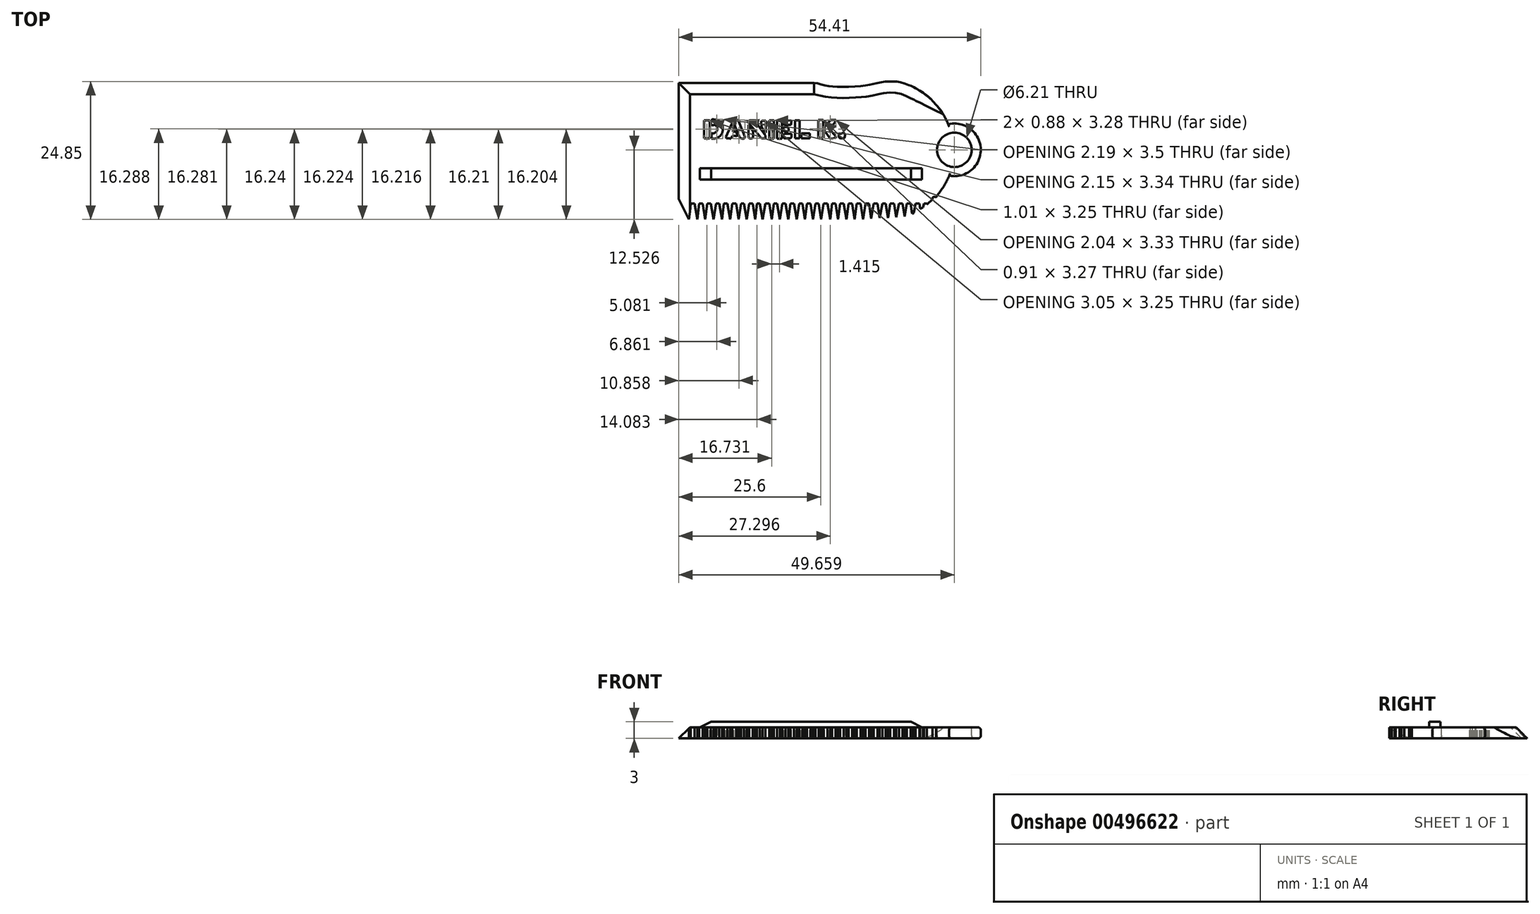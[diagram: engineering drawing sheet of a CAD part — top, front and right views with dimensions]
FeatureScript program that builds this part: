
annotation { "Feature Type Name" : "Feature", "Feature Type Description" : "" }
export const myFeature = defineFeature(function(context is Context, id is Id, definition is map)
    precondition{}
    {
        {
            var Q0;
            Q0=qCreatedBy(makeId("Top.planeOp"),FACE);
            var sketch = newSketch(context, id + "F0", { "sketchPlane" : qUnion([Q0])});
            skLineSegment(sketch, "E0", {"start": v(1.4, 38.48) * mm, "end": v(1.4, 17.59) * mm});
            skLineSegment(sketch, "E1", {"start": v(1.4, 17.59) * mm, "end": v(3.24, 13.91) * mm});
            skLineSegment(sketch, "E2", {"start": v(3.24, 13.91) * mm, "end": v(3.59, 16.75) * mm});
            skLineSegment(sketch, "E3", {"start": v(3.59, 16.75) * mm, "end": v(4.26, 16.75) * mm});
            skLineSegment(sketch, "E4", {"start": v(4.26, 16.75) * mm, "end": v(4.74, 13.91) * mm});
            skLineSegment(sketch, "E5", {"start": v(4.74, 13.91) * mm, "end": v(5.11, 16.75) * mm});
            skLineSegment(sketch, "E6", {"start": v(5.11, 16.75) * mm, "end": v(5.73, 16.75) * mm});
            skLineSegment(sketch, "E7", {"start": v(5.73, 16.75) * mm, "end": v(6.2, 13.91) * mm});
            skLineSegment(sketch, "E8", {"start": v(6.2, 13.91) * mm, "end": v(6.56, 16.75) * mm});
            skLineSegment(sketch, "E9", {"start": v(6.56, 16.75) * mm, "end": v(7.2, 16.75) * mm});
            skLineSegment(sketch, "E10", {"start": v(7.2, 16.75) * mm, "end": v(7.71, 13.91) * mm});
            skLineSegment(sketch, "E11", {"start": v(7.71, 13.91) * mm, "end": v(8.14, 16.75) * mm});
            skLineSegment(sketch, "E12", {"start": v(8.14, 16.75) * mm, "end": v(8.7, 16.75) * mm});
            skLineSegment(sketch, "E13", {"start": v(8.7, 16.75) * mm, "end": v(9.2, 13.91) * mm});
            skLineSegment(sketch, "E14", {"start": v(9.2, 13.91) * mm, "end": v(9.56, 16.75) * mm});
            skLineSegment(sketch, "E15", {"start": v(9.56, 16.75) * mm, "end": v(10.18, 16.75) * mm});
            skLineSegment(sketch, "E16", {"start": v(10.18, 16.75) * mm, "end": v(10.7, 13.91) * mm});
            skLineSegment(sketch, "E17", {"start": v(10.7, 13.91) * mm, "end": v(11.07, 16.75) * mm});
            skLineSegment(sketch, "E18", {"start": v(11.07, 16.75) * mm, "end": v(11.75, 16.75) * mm});
            skLineSegment(sketch, "E19", {"start": v(11.75, 16.75) * mm, "end": v(12.19, 13.91) * mm});
            skLineSegment(sketch, "E20", {"start": v(12.19, 13.91) * mm, "end": v(12.62, 16.75) * mm});
            skLineSegment(sketch, "E21", {"start": v(12.62, 16.75) * mm, "end": v(13.15, 16.75) * mm});
            skLineSegment(sketch, "E22", {"start": v(13.15, 16.75) * mm, "end": v(13.65, 13.91) * mm});
            skLineSegment(sketch, "E23", {"start": v(13.65, 13.91) * mm, "end": v(14.08, 16.75) * mm});
            skLineSegment(sketch, "E24", {"start": v(14.08, 16.75) * mm, "end": v(14.73, 16.75) * mm});
            skLineSegment(sketch, "E25", {"start": v(14.73, 16.75) * mm, "end": v(15.17, 13.91) * mm});
            skLineSegment(sketch, "E26", {"start": v(15.17, 13.91) * mm, "end": v(15.5, 16.75) * mm});
            skLineSegment(sketch, "E27", {"start": v(15.5, 16.75) * mm, "end": v(16.04, 16.75) * mm});
            skLineSegment(sketch, "E28", {"start": v(16.04, 16.75) * mm, "end": v(16.54, 13.91) * mm});
            skLineSegment(sketch, "E29", {"start": v(16.54, 13.91) * mm, "end": v(17.03, 16.75) * mm});
            skLineSegment(sketch, "E30", {"start": v(17.03, 16.75) * mm, "end": v(17.72, 16.75) * mm});
            skLineSegment(sketch, "E31", {"start": v(17.72, 16.75) * mm, "end": v(18.19, 13.91) * mm});
            skLineSegment(sketch, "E32", {"start": v(18.19, 13.91) * mm, "end": v(18.52, 16.75) * mm});
            skLineSegment(sketch, "E33", {"start": v(18.52, 16.75) * mm, "end": v(19.15, 16.75) * mm});
            skLineSegment(sketch, "E34", {"start": v(19.15, 16.75) * mm, "end": v(19.66, 13.91) * mm});
            skLineSegment(sketch, "E35", {"start": v(19.66, 13.91) * mm, "end": v(20.08, 16.75) * mm});
            skLineSegment(sketch, "E36", {"start": v(20.08, 16.75) * mm, "end": v(20.65, 16.75) * mm});
            skLineSegment(sketch, "E37", {"start": v(20.65, 16.75) * mm, "end": v(21.13, 13.91) * mm});
            skLineSegment(sketch, "E38", {"start": v(21.13, 13.91) * mm, "end": v(21.56, 16.75) * mm});
            skLineSegment(sketch, "E39", {"start": v(21.56, 16.75) * mm, "end": v(22.17, 16.75) * mm});
            skLineSegment(sketch, "E40", {"start": v(22.17, 16.75) * mm, "end": v(22.67, 13.91) * mm});
            skLineSegment(sketch, "E41", {"start": v(22.67, 13.91) * mm, "end": v(23.1, 16.75) * mm});
            skLineSegment(sketch, "E42", {"start": v(23.1, 16.75) * mm, "end": v(23.68, 16.75) * mm});
            skLineSegment(sketch, "E43", {"start": v(23.68, 16.75) * mm, "end": v(24.12, 13.91) * mm});
            skLineSegment(sketch, "E44", {"start": v(24.12, 13.91) * mm, "end": v(24.54, 16.75) * mm});
            skLineSegment(sketch, "E45", {"start": v(24.54, 16.75) * mm, "end": v(25.15, 16.75) * mm});
            skLineSegment(sketch, "E46", {"start": v(25.15, 16.75) * mm, "end": v(25.59, 13.91) * mm});
            skLineSegment(sketch, "E47", {"start": v(25.59, 13.91) * mm, "end": v(26.01, 16.75) * mm});
            skLineSegment(sketch, "E48", {"start": v(26.01, 16.75) * mm, "end": v(26.63, 16.75) * mm});
            skLineSegment(sketch, "E49", {"start": v(26.63, 16.75) * mm, "end": v(27.06, 13.91) * mm});
            skLineSegment(sketch, "E50", {"start": v(27.06, 13.91) * mm, "end": v(27.49, 16.75) * mm});
            skLineSegment(sketch, "E51", {"start": v(27.49, 16.75) * mm, "end": v(28.19, 16.75) * mm});
            skLineSegment(sketch, "E52", {"start": v(28.19, 16.75) * mm, "end": v(28.7, 13.91) * mm});
            skLineSegment(sketch, "E53", {"start": v(28.7, 13.91) * mm, "end": v(29.03, 16.75) * mm});
            skLineSegment(sketch, "E54", {"start": v(29.03, 16.75) * mm, "end": v(29.65, 16.75) * mm});
            skLineSegment(sketch, "E55", {"start": v(29.65, 16.75) * mm, "end": v(30.09, 13.91) * mm});
            skLineSegment(sketch, "E56", {"start": v(30.09, 13.91) * mm, "end": v(30.51, 16.75) * mm});
            skLineSegment(sketch, "E57", {"start": v(30.51, 16.75) * mm, "end": v(31.1, 16.75) * mm});
            skLineSegment(sketch, "E58", {"start": v(31.1, 16.75) * mm, "end": v(31.62, 13.91) * mm});
            skLineSegment(sketch, "E59", {"start": v(31.62, 13.91) * mm, "end": v(32.04, 16.75) * mm});
            skLineSegment(sketch, "E60", {"start": v(32.04, 16.75) * mm, "end": v(32.65, 16.75) * mm});
            skLineSegment(sketch, "E61", {"start": v(32.65, 16.75) * mm, "end": v(33.08, 13.91) * mm});
            skLineSegment(sketch, "E62", {"start": v(33.08, 13.91) * mm, "end": v(33.5, 16.75) * mm});
            skLineSegment(sketch, "E63", {"start": v(33.5, 16.75) * mm, "end": v(34.2, 16.75) * mm});
            skLineSegment(sketch, "E64", {"start": v(34.2, 16.75) * mm, "end": v(34.64, 13.91) * mm});
            skLineSegment(sketch, "E65", {"start": v(34.64, 13.91) * mm, "end": v(35.07, 16.75) * mm});
            skLineSegment(sketch, "E66", {"start": v(35.07, 16.75) * mm, "end": v(35.67, 16.75) * mm});
            skLineSegment(sketch, "E67", {"start": v(35.67, 16.75) * mm, "end": v(36.09, 14.06) * mm});
            skLineSegment(sketch, "E68", {"start": v(36.09, 14.06) * mm, "end": v(36.54, 16.75) * mm});
            skLineSegment(sketch, "E69", {"start": v(36.54, 16.75) * mm, "end": v(37.2, 16.75) * mm});
            skLineSegment(sketch, "E70", {"start": v(37.2, 16.75) * mm, "end": v(37.6, 14.13) * mm});
            skLineSegment(sketch, "E71", {"start": v(37.6, 14.13) * mm, "end": v(38.1, 16.75) * mm});
            skLineSegment(sketch, "E72", {"start": v(38.1, 16.75) * mm, "end": v(38.7, 16.75) * mm});
            skLineSegment(sketch, "E73", {"start": v(38.7, 16.75) * mm, "end": v(39.13, 14.13) * mm});
            skLineSegment(sketch, "E74", {"start": v(39.13, 14.13) * mm, "end": v(39.53, 16.75) * mm});
            skLineSegment(sketch, "E75", {"start": v(39.53, 16.75) * mm, "end": v(40.22, 16.75) * mm});
            skLineSegment(sketch, "E76", {"start": v(40.22, 16.75) * mm, "end": v(40.56, 14.29) * mm});
            skLineSegment(sketch, "E77", {"start": v(40.56, 14.29) * mm, "end": v(41.08, 16.75) * mm});
            skLineSegment(sketch, "E78", {"start": v(41.08, 16.75) * mm, "end": v(41.73, 16.75) * mm});
            skLineSegment(sketch, "E79", {"start": v(41.73, 16.75) * mm, "end": v(42.09, 14.41) * mm});
            skLineSegment(sketch, "E80", {"start": v(42.09, 14.41) * mm, "end": v(42.47, 16.75) * mm});
            skLineSegment(sketch, "E81", {"start": v(42.47, 16.75) * mm, "end": v(43.17, 16.75) * mm});
            skLineSegment(sketch, "E82", {"start": v(43.17, 16.75) * mm, "end": v(43.44, 14.9) * mm});
            skLineSegment(sketch, "E83", {"start": v(43.44, 14.9) * mm, "end": v(43.76, 15.1) * mm});
            skLineSegment(sketch, "E84", {"start": v(43.76, 15.1) * mm, "end": v(44.08, 16.75) * mm});
            skLineSegment(sketch, "E85", {"start": v(44.08, 16.75) * mm, "end": v(44.76, 16.75) * mm});
            skLineSegment(sketch, "E86", {"start": v(44.76, 16.75) * mm, "end": v(44.93, 15.78) * mm});
            skLineSegment(sketch, "E87", {"start": v(44.93, 15.78) * mm, "end": v(45.44, 16.08) * mm});
            skLineSegment(sketch, "E88", {"start": v(45.44, 16.08) * mm, "end": v(45.57, 16.75) * mm});
            skLineSegment(sketch, "E89", {"start": v(45.57, 16.75) * mm, "end": v(46.13, 16.75) * mm});
            skLineSegment(sketch, "E90", {"start": v(46.13, 16.75) * mm, "end": v(46.14, 16.6) * mm});
            skLineSegment(sketch, "E91", {"start": v(46.14, 16.6) * mm, "end": v(47.16, 17.52) * mm});
            skFitSpline(sketch, "E92", {"points": [v(1.4, 38.48) * mm, v(25.8, 38.48) * mm], "startDerivative": vector(24.39, 0) * mm, "endDerivative": vector(24.39, 0) * mm});
            skFitSpline(sketch, "E93", {"points": [v(25.8, 38.48) * mm, v(26.58, 38.37) * mm, v(27.86, 38) * mm, v(28.99, 37.85) * mm, v(30.77, 37.77) * mm, v(33.35, 37.86) * mm, v(35.53, 38.11) * mm, v(37.69, 38.6) * mm, v(39.09, 38.74) * mm, v(40.12, 38.76) * mm, v(41.15, 38.65) * mm, v(42.64, 38.2) * mm, v(43.17, 37.98) * mm, v(43.74, 37.71) * mm], "startDerivative": vector(12.37, -1.09) * mm, "endDerivative": vector(11.2, -5.59) * mm});
            skFitSpline(sketch, "E94", {"points": [v(43.74, 37.71) * mm, v(44.4, 37.35) * mm, v(45.39, 36.71) * mm, v(46.72, 35.7) * mm, v(47.62, 34.73) * mm, v(48.45, 33.74) * mm, v(49.36, 32.3) * mm, v(50.43, 29.83) * mm, v(51.02, 26.47) * mm, v(50.52, 22.9) * mm, v(49.43, 20.3) * mm, v(47.83, 18) * mm], "startDerivative": vector(11.48, -6.03) * mm, "endDerivative": vector(-15.82, -21.1) * mm});
            skFitSpline(sketch, "E95", {"points": [v(47.83, 18) * mm, v(47.76, 17.93) * mm], "startDerivative": vector(-0.07, -0.07) * mm, "endDerivative": vector(-0.07, -0.07) * mm});
            skFitSpline(sketch, "E96", {"points": [v(47.76, 17.93) * mm, v(47.6, 17.94) * mm, v(47.35, 17.95) * mm, v(47.23, 17.91) * mm, v(47.16, 17.82) * mm, v(47.15, 17.72) * mm, v(47.15, 17.6) * mm, v(47.16, 17.52) * mm], "startDerivative": vector(-0.96, 0.1) * mm, "endDerivative": vector(0.06, -0.72) * mm});
            skSolve(sketch);
        }
        {
            var Q0;
            Q0 = qSketchRegion(id + "F0", true);
            extrude(context, id + "F1", {"entities" : qUnion([Q0]), "depth" : 2 * mm, "offsetDistance" : 25 * mm});
        }
        {
            var Q0;
            Q0=makeQuery(id+"F1.opExtrude","CAP_EDGE",EDGE,{"disambiguationData":[OSD([sQuery(id+"F0.wireOp",EDGE,"E0")])],"isStart":false});
            var Q1;
            Q1=makeQuery(id+"F1.opExtrude","CAP_EDGE",EDGE,{"disambiguationData":[OSD([sQuery(id+"F0.wireOp",EDGE,"E92")])],"isStart":false});
            chamfer(context, id + "F2", {"entities" : qUnion([Q0, Q1]), "chamferType" : ChamferType.TWO_OFFSETS, "width1" : 2 * mm, "oppositeDirection" : false, "width2" : 2 * mm, "tangentPropagation" : true});
        }
        {
            var Q0;
            Q0=makeQuery(id+"F1.opExtrude","CAP_FACE",FACE,{"disambiguationData":[OSD([sQuery(id+"F0.wireOp",EDGE,"E0"),sQuery(id+"F0.wireOp",EDGE,"E1"),sQuery(id+"F0.wireOp",EDGE,"E2"),sQuery(id+"F0.wireOp",EDGE,"E3"),sQuery(id+"F0.wireOp",EDGE,"E4"),sQuery(id+"F0.wireOp",EDGE,"E5"),sQuery(id+"F0.wireOp",EDGE,"E6"),sQuery(id+"F0.wireOp",EDGE,"E7"),sQuery(id+"F0.wireOp",EDGE,"E8"),sQuery(id+"F0.wireOp",EDGE,"E9"),sQuery(id+"F0.wireOp",EDGE,"E10"),sQuery(id+"F0.wireOp",EDGE,"E11"),sQuery(id+"F0.wireOp",EDGE,"E12"),sQuery(id+"F0.wireOp",EDGE,"E13"),sQuery(id+"F0.wireOp",EDGE,"E14"),sQuery(id+"F0.wireOp",EDGE,"E15"),sQuery(id+"F0.wireOp",EDGE,"E16"),sQuery(id+"F0.wireOp",EDGE,"E17"),sQuery(id+"F0.wireOp",EDGE,"E18"),sQuery(id+"F0.wireOp",EDGE,"E19"),sQuery(id+"F0.wireOp",EDGE,"E20"),sQuery(id+"F0.wireOp",EDGE,"E21"),sQuery(id+"F0.wireOp",EDGE,"E22"),sQuery(id+"F0.wireOp",EDGE,"E23"),sQuery(id+"F0.wireOp",EDGE,"E24"),sQuery(id+"F0.wireOp",EDGE,"E25"),sQuery(id+"F0.wireOp",EDGE,"E26"),sQuery(id+"F0.wireOp",EDGE,"E27"),sQuery(id+"F0.wireOp",EDGE,"E28"),sQuery(id+"F0.wireOp",EDGE,"E29"),sQuery(id+"F0.wireOp",EDGE,"E30"),sQuery(id+"F0.wireOp",EDGE,"E31"),sQuery(id+"F0.wireOp",EDGE,"E32"),sQuery(id+"F0.wireOp",EDGE,"E33"),sQuery(id+"F0.wireOp",EDGE,"E34"),sQuery(id+"F0.wireOp",EDGE,"E35"),sQuery(id+"F0.wireOp",EDGE,"E36"),sQuery(id+"F0.wireOp",EDGE,"E37"),sQuery(id+"F0.wireOp",EDGE,"E38"),sQuery(id+"F0.wireOp",EDGE,"E39"),sQuery(id+"F0.wireOp",EDGE,"E40"),sQuery(id+"F0.wireOp",EDGE,"E41"),sQuery(id+"F0.wireOp",EDGE,"E42"),sQuery(id+"F0.wireOp",EDGE,"E43"),sQuery(id+"F0.wireOp",EDGE,"E44"),sQuery(id+"F0.wireOp",EDGE,"E45"),sQuery(id+"F0.wireOp",EDGE,"E46"),sQuery(id+"F0.wireOp",EDGE,"E47"),sQuery(id+"F0.wireOp",EDGE,"E48"),sQuery(id+"F0.wireOp",EDGE,"E49"),sQuery(id+"F0.wireOp",EDGE,"E50"),sQuery(id+"F0.wireOp",EDGE,"E51"),sQuery(id+"F0.wireOp",EDGE,"E52"),sQuery(id+"F0.wireOp",EDGE,"E53"),sQuery(id+"F0.wireOp",EDGE,"E54"),sQuery(id+"F0.wireOp",EDGE,"E55"),sQuery(id+"F0.wireOp",EDGE,"E56"),sQuery(id+"F0.wireOp",EDGE,"E57"),sQuery(id+"F0.wireOp",EDGE,"E58"),sQuery(id+"F0.wireOp",EDGE,"E59"),sQuery(id+"F0.wireOp",EDGE,"E60"),sQuery(id+"F0.wireOp",EDGE,"E61"),sQuery(id+"F0.wireOp",EDGE,"E62"),sQuery(id+"F0.wireOp",EDGE,"E63"),sQuery(id+"F0.wireOp",EDGE,"E64"),sQuery(id+"F0.wireOp",EDGE,"E65"),sQuery(id+"F0.wireOp",EDGE,"E66"),sQuery(id+"F0.wireOp",EDGE,"E67"),sQuery(id+"F0.wireOp",EDGE,"E68"),sQuery(id+"F0.wireOp",EDGE,"E69"),sQuery(id+"F0.wireOp",EDGE,"E70"),sQuery(id+"F0.wireOp",EDGE,"E71"),sQuery(id+"F0.wireOp",EDGE,"E72"),sQuery(id+"F0.wireOp",EDGE,"E73"),sQuery(id+"F0.wireOp",EDGE,"E74"),sQuery(id+"F0.wireOp",EDGE,"E75"),sQuery(id+"F0.wireOp",EDGE,"E76"),sQuery(id+"F0.wireOp",EDGE,"E77"),sQuery(id+"F0.wireOp",EDGE,"E78"),sQuery(id+"F0.wireOp",EDGE,"E79"),sQuery(id+"F0.wireOp",EDGE,"E80"),sQuery(id+"F0.wireOp",EDGE,"E81"),sQuery(id+"F0.wireOp",EDGE,"E82"),sQuery(id+"F0.wireOp",EDGE,"E83"),sQuery(id+"F0.wireOp",EDGE,"E84"),sQuery(id+"F0.wireOp",EDGE,"E85"),sQuery(id+"F0.wireOp",EDGE,"E86"),sQuery(id+"F0.wireOp",EDGE,"E87"),sQuery(id+"F0.wireOp",EDGE,"E88"),sQuery(id+"F0.wireOp",EDGE,"E89"),sQuery(id+"F0.wireOp",EDGE,"E90"),sQuery(id+"F0.wireOp",EDGE,"E91"),sQuery(id+"F0.wireOp",EDGE,"E92"),sQuery(id+"F0.wireOp",EDGE,"E93"),sQuery(id+"F0.wireOp",EDGE,"E94"),sQuery(id+"F0.wireOp",EDGE,"E95"),sQuery(id+"F0.wireOp",EDGE,"E96")])],"isStart":false});
            var sketch = newSketch(context, id + "F3", { "sketchPlane" : qUnion([Q0])});
            skLineSegment(sketch, "E97", {"start": v(5.99, 31.77) * mm, "end": v(5.99, 28.53) * mm});
            skLineSegment(sketch, "E98", {"start": v(5.99, 28.53) * mm, "end": v(7, 28.53) * mm});
            skLineSegment(sketch, "E99", {"start": v(7, 28.53) * mm, "end": v(7, 31.77) * mm});
            skLineSegment(sketch, "E100", {"start": v(7, 31.77) * mm, "end": v(5.99, 31.77) * mm});
            skFitSpline(sketch, "E101", {"points": [v(7.44, 31.94) * mm, v(7.78, 31.91) * mm, v(8.32, 31.82) * mm, v(8.75, 31.62) * mm, v(9.03, 31.34) * mm, v(9.2, 31.04) * mm, v(9.32, 30.67) * mm, v(9.37, 30.21) * mm, v(9.34, 29.76) * mm, v(9.13, 29.24) * mm, v(8.8, 28.86) * mm, v(8.33, 28.58) * mm, v(7.8, 28.47) * mm, v(7.34, 28.44) * mm], "startDerivative": vector(4.8, -0.39) * mm, "endDerivative": vector(-5.87, -0.25) * mm});
            skFitSpline(sketch, "E102", {"points": [v(7.34, 28.44) * mm, v(7.34, 29.4) * mm], "startDerivative": vector(0, 0.96) * mm, "endDerivative": vector(0, 0.96) * mm});
            skFitSpline(sketch, "E103", {"points": [v(7.34, 29.4) * mm, v(7.63, 29.4) * mm, v(7.96, 29.52) * mm, v(8.28, 29.81) * mm, v(8.35, 30.22) * mm, v(8.27, 30.62) * mm, v(8.1, 30.82) * mm, v(7.9, 30.91) * mm, v(7.69, 30.9) * mm, v(7.54, 30.87) * mm, v(7.34, 30.89) * mm, v(7.17, 31.17) * mm, v(7.23, 31.58) * mm, v(7.44, 31.94) * mm], "startDerivative": vector(3.85, -0.27) * mm, "endDerivative": vector(2.58, 3.9) * mm});
            skFitSpline(sketch, "E104", {"points": [v(10.98, 31.2) * mm, v(9.92, 28.8) * mm], "startDerivative": vector(-1.06, -2.41) * mm, "endDerivative": vector(-1.06, -2.41) * mm});
            skFitSpline(sketch, "E105", {"points": [v(9.92, 28.8) * mm, v(9.98, 28.53) * mm], "startDerivative": vector(0.06, -0.27) * mm, "endDerivative": vector(0.06, -0.27) * mm});
            skFitSpline(sketch, "E106", {"points": [v(9.98, 28.53) * mm, v(10.55, 28.53) * mm], "startDerivative": vector(0.57, 0) * mm, "endDerivative": vector(0.57, 0) * mm});
            skFitSpline(sketch, "E107", {"points": [v(10.55, 28.53) * mm, v(10.58, 28.52) * mm, v(10.61, 28.5) * mm, v(10.65, 28.46) * mm], "startDerivative": vector(0.09, -0.02) * mm, "endDerivative": vector(0.08, -0.13) * mm});
            skFitSpline(sketch, "E108", {"points": [v(10.65, 28.46) * mm, v(10.79, 28.46) * mm], "startDerivative": vector(0.14, 0) * mm, "endDerivative": vector(0.14, 0) * mm});
            skFitSpline(sketch, "E109", {"points": [v(10.79, 28.46) * mm, v(11.05, 28.96) * mm], "startDerivative": vector(0.26, 0.5) * mm, "endDerivative": vector(0.26, 0.5) * mm});
            skFitSpline(sketch, "E110", {"points": [v(11.05, 28.96) * mm, v(11.68, 28.96) * mm], "startDerivative": vector(0.63, 0) * mm, "endDerivative": vector(0.63, 0) * mm});
            skFitSpline(sketch, "E111", {"points": [v(11.68, 28.96) * mm, v(11.72, 28.91) * mm, v(11.82, 28.9) * mm], "startDerivative": vector(0.09, -0.13) * mm, "endDerivative": vector(0.2, 0.02) * mm});
            skFitSpline(sketch, "E112", {"points": [v(11.82, 28.9) * mm, v(11.94, 29.03) * mm], "startDerivative": vector(0.12, 0.12) * mm, "endDerivative": vector(0.12, 0.12) * mm});
            skFitSpline(sketch, "E113", {"points": [v(11.94, 29.03) * mm, v(11.94, 29.22) * mm], "startDerivative": vector(0, 0.2) * mm, "endDerivative": vector(0, 0.2) * mm});
            skLineSegment(sketch, "E114", {"start": v(11.94, 29.22) * mm, "end": v(11.72, 29.69) * mm});
            skLineSegment(sketch, "E115", {"start": v(11.72, 29.69) * mm, "end": v(11.22, 29.71) * mm});
            skLineSegment(sketch, "E116", {"start": v(10.98, 31.2) * mm, "end": v(11.04, 31.2) * mm});
            skLineSegment(sketch, "E117", {"start": v(11.04, 31.2) * mm, "end": v(11.4, 30.35) * mm});
            skLineSegment(sketch, "E118", {"start": v(11.4, 30.35) * mm, "end": v(11.2, 29.75) * mm});
            skLineSegment(sketch, "E119", {"start": v(11.2, 29.75) * mm, "end": v(11.22, 29.71) * mm});
            skLineSegment(sketch, "E120", {"start": v(11.2, 31.56) * mm, "end": v(12.4, 28.62) * mm});
            skLineSegment(sketch, "E121", {"start": v(12.13, 31.77) * mm, "end": v(13.34, 28.73) * mm});
            skFitSpline(sketch, "E122", {"points": [v(12.4, 28.62) * mm, v(12.57, 28.54) * mm, v(12.77, 28.47) * mm, v(13, 28.45) * mm, v(13.16, 28.46) * mm], "startDerivative": vector(0.67, -0.35) * mm, "endDerivative": vector(0.72, 0.05) * mm});
            skFitSpline(sketch, "E123", {"points": [v(13.16, 28.46) * mm, v(13.27, 28.55) * mm, v(13.34, 28.66) * mm, v(13.34, 28.73) * mm], "startDerivative": vector(0.3, 0.21) * mm, "endDerivative": vector(0, 0.25) * mm});
            skFitSpline(sketch, "E124", {"points": [v(12.13, 31.77) * mm, v(12, 31.8) * mm, v(11.6, 31.8) * mm, v(11.34, 31.78) * mm, v(11.27, 31.7) * mm, v(11.2, 31.56) * mm], "startDerivative": vector(-0.7, 0.18) * mm, "endDerivative": vector(-0.45, -0.87) * mm});
            skLineSegment(sketch, "E125", {"start": v(13.97, 30.95) * mm, "end": v(13.97, 28.64) * mm});
            skFitSpline(sketch, "E126", {"points": [v(13.97, 28.64) * mm, v(14.15, 28.52) * mm, v(14.55, 28.49) * mm, v(14.75, 28.57) * mm], "startDerivative": vector(0.49, -0.5) * mm, "endDerivative": vector(0.6, 0.32) * mm});
            skFitSpline(sketch, "E127", {"points": [v(14.75, 28.57) * mm, v(14.8, 28.83) * mm], "startDerivative": vector(0.06, 0.26) * mm, "endDerivative": vector(0.06, 0.26) * mm});
            skFitSpline(sketch, "E128", {"points": [v(14.8, 28.83) * mm, v(14.8, 29.75) * mm], "startDerivative": vector(0, 1.1) * mm, "endDerivative": vector(0, 1.1) * mm});
            skFitSpline(sketch, "E129", {"points": [v(14.8, 29.75) * mm, v(13.97, 30.95) * mm], "startDerivative": vector(-0.84, 1.01) * mm, "endDerivative": vector(-0.84, 1.01) * mm});
            skFitSpline(sketch, "E130", {"points": [v(13.97, 31.38) * mm, v(16.3, 28.49) * mm], "startDerivative": vector(2.28, -2.89) * mm, "endDerivative": vector(2.28, -2.89) * mm});
            skFitSpline(sketch, "E131", {"points": [v(16.3, 28.49) * mm, v(17.02, 28.49) * mm], "startDerivative": vector(0.77, 0) * mm, "endDerivative": vector(0.77, 0) * mm});
            skFitSpline(sketch, "E132", {"points": [v(17.02, 28.49) * mm, v(17.02, 29) * mm], "startDerivative": vector(0, 0.52) * mm, "endDerivative": vector(0, 0.52) * mm});
            skFitSpline(sketch, "E133", {"points": [v(17.02, 29) * mm, v(15.06, 31.74) * mm], "startDerivative": vector(-1.96, 2.73) * mm, "endDerivative": vector(-1.96, 2.73) * mm});
            skFitSpline(sketch, "E134", {"points": [v(15.06, 31.74) * mm, v(14.2, 31.74) * mm], "startDerivative": vector(-0.87, 0) * mm, "endDerivative": vector(-0.87, 0) * mm});
            skFitSpline(sketch, "E135", {"points": [v(14.2, 31.74) * mm, v(14.07, 31.66) * mm, v(13.97, 31.53) * mm, v(13.97, 31.38) * mm], "startDerivative": vector(-0.39, -0.2) * mm, "endDerivative": vector(0.07, -0.47) * mm});
            skFitSpline(sketch, "E136", {"points": [v(16.3, 30.6) * mm, v(17.1, 29.5) * mm], "startDerivative": vector(0.85, -0.87) * mm, "endDerivative": vector(0.85, -0.87) * mm});
            skFitSpline(sketch, "E137", {"points": [v(17.1, 29.5) * mm, v(17.1, 31.7) * mm], "startDerivative": vector(0, 2.2) * mm, "endDerivative": vector(0, 2.2) * mm});
            skFitSpline(sketch, "E138", {"points": [v(17.1, 31.7) * mm, v(16.49, 31.7) * mm], "startDerivative": vector(-0.61, 0) * mm, "endDerivative": vector(-0.61, 0) * mm});
            skFitSpline(sketch, "E139", {"points": [v(16.49, 31.7) * mm, v(16.36, 31.63) * mm, v(16.3, 31.56) * mm], "startDerivative": vector(-0.26, -0.1) * mm, "endDerivative": vector(-0.12, -0.17) * mm});
            skFitSpline(sketch, "E140", {"points": [v(16.3, 31.56) * mm, v(16.3, 30.6) * mm], "startDerivative": vector(-0.04, -1.19) * mm, "endDerivative": vector(-0.04, -1.19) * mm});
            skLineSegment(sketch, "E141", {"start": v(17.7, 31.76) * mm, "end": v(17.7, 28.48) * mm});
            skLineSegment(sketch, "E142", {"start": v(17.7, 28.48) * mm, "end": v(18.58, 28.48) * mm});
            skLineSegment(sketch, "E143", {"start": v(18.58, 28.48) * mm, "end": v(18.58, 31.76) * mm});
            skLineSegment(sketch, "E144", {"start": v(18.58, 31.76) * mm, "end": v(17.7, 31.76) * mm});
            skLineSegment(sketch, "E145", {"start": v(19.12, 28.48) * mm, "end": v(20, 28.48) * mm});
            skLineSegment(sketch, "E146", {"start": v(20, 28.48) * mm, "end": v(20, 31.76) * mm});
            skLineSegment(sketch, "E147", {"start": v(20, 31.76) * mm, "end": v(19.12, 31.76) * mm});
            skLineSegment(sketch, "E148", {"start": v(19.12, 31.76) * mm, "end": v(19.12, 28.48) * mm});
            skFitSpline(sketch, "E149", {"points": [v(20.4, 30.52) * mm, v(21.09, 30.5) * mm], "startDerivative": vector(0.69, -0.02) * mm, "endDerivative": vector(0.69, -0.02) * mm});
            skFitSpline(sketch, "E150", {"points": [v(21.09, 30.5) * mm, v(21.17, 30.3) * mm, v(21.2, 30.02) * mm, v(21.09, 29.8) * mm], "startDerivative": vector(0.3, -0.57) * mm, "endDerivative": vector(-0.4, -0.6) * mm});
            skFitSpline(sketch, "E151", {"points": [v(21.09, 29.8) * mm, v(20.44, 29.8) * mm], "startDerivative": vector(-0.65, 0) * mm, "endDerivative": vector(-0.65, 0) * mm});
            skFitSpline(sketch, "E152", {"points": [v(20.44, 29.8) * mm, v(20.33, 29.89) * mm, v(20.23, 30.09) * mm, v(20.3, 30.35) * mm, v(20.4, 30.52) * mm], "startDerivative": vector(-0.55, 0.32) * mm, "endDerivative": vector(0.38, 0.62) * mm});
            skFitSpline(sketch, "E153", {"points": [v(20.53, 31.71) * mm, v(21.62, 31.72) * mm], "startDerivative": vector(1.1, 0) * mm, "endDerivative": vector(1.1, 0) * mm});
            skFitSpline(sketch, "E154", {"points": [v(21.62, 31.72) * mm, v(21.7, 31.58) * mm, v(21.7, 31.35) * mm, v(21.67, 31.04) * mm, v(21.56, 30.95) * mm], "startDerivative": vector(0.4, -0.58) * mm, "endDerivative": vector(-0.6, -0.33) * mm});
            skFitSpline(sketch, "E155", {"points": [v(21.56, 30.95) * mm, v(20.44, 30.95) * mm], "startDerivative": vector(-1.12, 0) * mm, "endDerivative": vector(-1.12, 0) * mm});
            skFitSpline(sketch, "E156", {"points": [v(20.44, 30.95) * mm, v(20.33, 31.06) * mm, v(20.3, 31.27) * mm, v(20.4, 31.54) * mm, v(20.53, 31.71) * mm], "startDerivative": vector(-0.57, 0.43) * mm, "endDerivative": vector(0.5, 0.63) * mm});
            skFitSpline(sketch, "E157", {"points": [v(20.4, 29.33) * mm, v(21.68, 29.33) * mm], "startDerivative": vector(1.28, 0) * mm, "endDerivative": vector(1.28, 0) * mm});
            skFitSpline(sketch, "E158", {"points": [v(21.68, 29.33) * mm, v(21.72, 29.25) * mm, v(21.75, 28.94) * mm, v(21.72, 28.7) * mm, v(21.56, 28.54) * mm], "startDerivative": vector(0.27, -0.4) * mm, "endDerivative": vector(-0.76, -0.58) * mm});
            skFitSpline(sketch, "E159", {"points": [v(21.56, 28.54) * mm, v(20.4, 28.54) * mm], "startDerivative": vector(-1.16, 0) * mm, "endDerivative": vector(-1.16, 0) * mm});
            skFitSpline(sketch, "E160", {"points": [v(20.4, 28.54) * mm, v(20.32, 28.63) * mm, v(20.26, 28.78) * mm, v(20.27, 28.98) * mm, v(20.34, 29.18) * mm, v(20.4, 29.33) * mm], "startDerivative": vector(-0.52, 0.46) * mm, "endDerivative": vector(0.33, 0.72) * mm});
            skLineSegment(sketch, "E161", {"start": v(22.38, 31.74) * mm, "end": v(22.38, 28.52) * mm});
            skLineSegment(sketch, "E162", {"start": v(22.38, 28.52) * mm, "end": v(23.22, 28.52) * mm});
            skLineSegment(sketch, "E163", {"start": v(23.22, 28.52) * mm, "end": v(23.22, 31.74) * mm});
            skLineSegment(sketch, "E164", {"start": v(23.22, 31.74) * mm, "end": v(22.38, 31.74) * mm});
            skLineSegment(sketch, "E165", {"start": v(23.5, 29.38) * mm, "end": v(23.5, 28.52) * mm});
            skLineSegment(sketch, "E166", {"start": v(23.5, 28.52) * mm, "end": v(25.05, 28.52) * mm});
            skLineSegment(sketch, "E167", {"start": v(25.05, 28.52) * mm, "end": v(25.05, 29.38) * mm});
            skLineSegment(sketch, "E168", {"start": v(25.05, 29.38) * mm, "end": v(23.5, 29.38) * mm});
            skLineSegment(sketch, "E169", {"start": v(26.55, 31.83) * mm, "end": v(26.55, 28.56) * mm});
            skLineSegment(sketch, "E170", {"start": v(26.55, 28.56) * mm, "end": v(27.47, 28.56) * mm});
            skLineSegment(sketch, "E171", {"start": v(27.47, 28.56) * mm, "end": v(27.47, 31.83) * mm});
            skLineSegment(sketch, "E172", {"start": v(27.47, 31.83) * mm, "end": v(26.55, 31.83) * mm});
            skLineSegment(sketch, "E173", {"start": v(27.69, 30.63) * mm, "end": v(27.69, 29.83) * mm});
            skLineSegment(sketch, "E174", {"start": v(27.69, 29.83) * mm, "end": v(28.68, 28.47) * mm});
            skLineSegment(sketch, "E175", {"start": v(28.68, 28.47) * mm, "end": v(29.73, 28.6) * mm});
            skFitSpline(sketch, "E176", {"points": [v(29.73, 28.6) * mm, v(29.73, 28.8) * mm], "startDerivative": vector(0, 0.21) * mm, "endDerivative": vector(0, 0.21) * mm});
            skFitSpline(sketch, "E177", {"points": [v(29.73, 28.8) * mm, v(28.58, 30.18) * mm], "startDerivative": vector(-1.15, 1.38) * mm, "endDerivative": vector(-1.15, 1.38) * mm});
            skFitSpline(sketch, "E178", {"points": [v(28.58, 30.18) * mm, v(29.73, 31.6) * mm], "startDerivative": vector(1.15, 1.42) * mm, "endDerivative": vector(1.15, 1.42) * mm});
            skFitSpline(sketch, "E179", {"points": [v(29.73, 31.6) * mm, v(29.73, 31.8) * mm], "startDerivative": vector(0, 0.2) * mm, "endDerivative": vector(0, 0.2) * mm});
            skFitSpline(sketch, "E180", {"points": [v(29.73, 31.8) * mm, v(28.81, 31.8) * mm], "startDerivative": vector(-0.91, 0) * mm, "endDerivative": vector(-0.91, 0) * mm});
            skFitSpline(sketch, "E181", {"points": [v(28.81, 31.8) * mm, v(27.69, 30.63) * mm], "startDerivative": vector(-1.13, -1.17) * mm, "endDerivative": vector(-1.13, -1.17) * mm});
            skFitSpline(sketch, "E182", {"points": [v(30.3, 29.34) * mm, v(30.3, 28.73) * mm, v(30.52, 28.52) * mm, v(31.26, 28.54) * mm, v(31.28, 28.6) * mm, v(31.33, 28.8) * mm, v(31.37, 29.14) * mm, v(31.28, 29.36) * mm, v(31, 29.46) * mm, v(30.86, 29.43) * mm, v(30.83, 29.38) * mm, v(30.52, 29.36) * mm, v(30.3, 29.34) * mm]});
            skSolve(sketch);
        }
        {
            var Q0;
            Q0=makeQuery(id+"F3.imprint","IMPRINT",FACE,{"disambiguationData":[TD([[makeQuery(id+"F3.imprint","IMPRINT",EDGE,{"derivedFrom":sQuery(id+"F3.wireOp",EDGE,"E97")}),1.0]])]});
            var Q1;
            Q1=makeQuery(id+"F3.imprint","IMPRINT",FACE,{"disambiguationData":[TD([[makeQuery(id+"F3.imprint","IMPRINT",EDGE,{"derivedFrom":sQuery(id+"F3.wireOp",EDGE,"E101")}),-1.0]])]});
            var Q2;
            Q2=makeQuery(id+"F3.imprint","IMPRINT",FACE,{"disambiguationData":[TD([[makeQuery(id+"F3.imprint","IMPRINT",EDGE,{"derivedFrom":sQuery(id+"F3.wireOp",EDGE,"E104")}),1.0]])]});
            var Q3;
            Q3=makeQuery(id+"F3.imprint","IMPRINT",FACE,{"disambiguationData":[TD([[makeQuery(id+"F3.imprint","IMPRINT",EDGE,{"derivedFrom":sQuery(id+"F3.wireOp",EDGE,"E120")}),1.0]])]});
            extrude(context, id + "F4", {"entities" : qUnion([Q0, Q1, Q2, Q3]), "operationType" : NewBodyOperationType.REMOVE, "oppositeDirection" : true, "depth" : 1 * mm, "offsetDistance" : 25 * mm});
        }
        {
            var Q0;
            Q0 = qSketchRegion(id + "F3", true);
            extrude(context, id + "F5", {"entities" : qUnion([Q0]), "operationType" : NewBodyOperationType.REMOVE, "oppositeDirection" : true, "depth" : 5 * mm, "offsetDistance" : 25 * mm});
        }
        {
            var Q0;
            Q0=makeQuery(id+"F1.opExtrude","CAP_FACE",FACE,{"disambiguationData":[OSD([sQuery(id+"F0.wireOp",EDGE,"E0"),sQuery(id+"F0.wireOp",EDGE,"E1"),sQuery(id+"F0.wireOp",EDGE,"E2"),sQuery(id+"F0.wireOp",EDGE,"E3"),sQuery(id+"F0.wireOp",EDGE,"E4"),sQuery(id+"F0.wireOp",EDGE,"E5"),sQuery(id+"F0.wireOp",EDGE,"E6"),sQuery(id+"F0.wireOp",EDGE,"E7"),sQuery(id+"F0.wireOp",EDGE,"E8"),sQuery(id+"F0.wireOp",EDGE,"E9"),sQuery(id+"F0.wireOp",EDGE,"E10"),sQuery(id+"F0.wireOp",EDGE,"E11"),sQuery(id+"F0.wireOp",EDGE,"E12"),sQuery(id+"F0.wireOp",EDGE,"E13"),sQuery(id+"F0.wireOp",EDGE,"E14"),sQuery(id+"F0.wireOp",EDGE,"E15"),sQuery(id+"F0.wireOp",EDGE,"E16"),sQuery(id+"F0.wireOp",EDGE,"E17"),sQuery(id+"F0.wireOp",EDGE,"E18"),sQuery(id+"F0.wireOp",EDGE,"E19"),sQuery(id+"F0.wireOp",EDGE,"E20"),sQuery(id+"F0.wireOp",EDGE,"E21"),sQuery(id+"F0.wireOp",EDGE,"E22"),sQuery(id+"F0.wireOp",EDGE,"E23"),sQuery(id+"F0.wireOp",EDGE,"E24"),sQuery(id+"F0.wireOp",EDGE,"E25"),sQuery(id+"F0.wireOp",EDGE,"E26"),sQuery(id+"F0.wireOp",EDGE,"E27"),sQuery(id+"F0.wireOp",EDGE,"E28"),sQuery(id+"F0.wireOp",EDGE,"E29"),sQuery(id+"F0.wireOp",EDGE,"E30"),sQuery(id+"F0.wireOp",EDGE,"E31"),sQuery(id+"F0.wireOp",EDGE,"E32"),sQuery(id+"F0.wireOp",EDGE,"E33"),sQuery(id+"F0.wireOp",EDGE,"E34"),sQuery(id+"F0.wireOp",EDGE,"E35"),sQuery(id+"F0.wireOp",EDGE,"E36"),sQuery(id+"F0.wireOp",EDGE,"E37"),sQuery(id+"F0.wireOp",EDGE,"E38"),sQuery(id+"F0.wireOp",EDGE,"E39"),sQuery(id+"F0.wireOp",EDGE,"E40"),sQuery(id+"F0.wireOp",EDGE,"E41"),sQuery(id+"F0.wireOp",EDGE,"E42"),sQuery(id+"F0.wireOp",EDGE,"E43"),sQuery(id+"F0.wireOp",EDGE,"E44"),sQuery(id+"F0.wireOp",EDGE,"E45"),sQuery(id+"F0.wireOp",EDGE,"E46"),sQuery(id+"F0.wireOp",EDGE,"E47"),sQuery(id+"F0.wireOp",EDGE,"E48"),sQuery(id+"F0.wireOp",EDGE,"E49"),sQuery(id+"F0.wireOp",EDGE,"E50"),sQuery(id+"F0.wireOp",EDGE,"E51"),sQuery(id+"F0.wireOp",EDGE,"E52"),sQuery(id+"F0.wireOp",EDGE,"E53"),sQuery(id+"F0.wireOp",EDGE,"E54"),sQuery(id+"F0.wireOp",EDGE,"E55"),sQuery(id+"F0.wireOp",EDGE,"E56"),sQuery(id+"F0.wireOp",EDGE,"E57"),sQuery(id+"F0.wireOp",EDGE,"E58"),sQuery(id+"F0.wireOp",EDGE,"E59"),sQuery(id+"F0.wireOp",EDGE,"E60"),sQuery(id+"F0.wireOp",EDGE,"E61"),sQuery(id+"F0.wireOp",EDGE,"E62"),sQuery(id+"F0.wireOp",EDGE,"E63"),sQuery(id+"F0.wireOp",EDGE,"E64"),sQuery(id+"F0.wireOp",EDGE,"E65"),sQuery(id+"F0.wireOp",EDGE,"E66"),sQuery(id+"F0.wireOp",EDGE,"E67"),sQuery(id+"F0.wireOp",EDGE,"E68"),sQuery(id+"F0.wireOp",EDGE,"E69"),sQuery(id+"F0.wireOp",EDGE,"E70"),sQuery(id+"F0.wireOp",EDGE,"E71"),sQuery(id+"F0.wireOp",EDGE,"E72"),sQuery(id+"F0.wireOp",EDGE,"E73"),sQuery(id+"F0.wireOp",EDGE,"E74"),sQuery(id+"F0.wireOp",EDGE,"E75"),sQuery(id+"F0.wireOp",EDGE,"E76"),sQuery(id+"F0.wireOp",EDGE,"E77"),sQuery(id+"F0.wireOp",EDGE,"E78"),sQuery(id+"F0.wireOp",EDGE,"E79"),sQuery(id+"F0.wireOp",EDGE,"E80"),sQuery(id+"F0.wireOp",EDGE,"E81"),sQuery(id+"F0.wireOp",EDGE,"E82"),sQuery(id+"F0.wireOp",EDGE,"E83"),sQuery(id+"F0.wireOp",EDGE,"E84"),sQuery(id+"F0.wireOp",EDGE,"E85"),sQuery(id+"F0.wireOp",EDGE,"E86"),sQuery(id+"F0.wireOp",EDGE,"E87"),sQuery(id+"F0.wireOp",EDGE,"E88"),sQuery(id+"F0.wireOp",EDGE,"E89"),sQuery(id+"F0.wireOp",EDGE,"E90"),sQuery(id+"F0.wireOp",EDGE,"E91"),sQuery(id+"F0.wireOp",EDGE,"E92"),sQuery(id+"F0.wireOp",EDGE,"E93"),sQuery(id+"F0.wireOp",EDGE,"E94"),sQuery(id+"F0.wireOp",EDGE,"E95"),sQuery(id+"F0.wireOp",EDGE,"E96")])],"isStart":false});
            var sketch = newSketch(context, id + "F6", { "sketchPlane" : qUnion([Q0])});
            skLineSegment(sketch, "E183.bottom", {"start": v(5.23, 21.1) * mm, "end": v(45.23, 21.1) * mm});
            skLineSegment(sketch, "E183.top", {"start": v(5.23, 23.1) * mm, "end": v(45.23, 23.1) * mm});
            skLineSegment(sketch, "E183.left", {"start": v(5.23, 21.1) * mm, "end": v(5.23, 23.1) * mm});
            skLineSegment(sketch, "E183.right", {"start": v(45.23, 21.1) * mm, "end": v(45.23, 23.1) * mm});
            skSolve(sketch);
        }
        {
            var Q0;
            Q0=makeQuery(id+"F6.imprint","IMPRINT",FACE,{"disambiguationData":[TD([[makeQuery(id+"F6.imprint","IMPRINT",EDGE,{"derivedFrom":sQuery(id+"F6.wireOp",EDGE,"E183.bottom")}),1.0]])]});
            extrude(context, id + "F7", {"entities" : qUnion([Q0]), "operationType" : NewBodyOperationType.ADD, "depth" : 1 * mm, "offsetDistance" : 25 * mm});
        }
        {
            var Q0;
            Q0=makeQuery(id+"F7.opExtrude","CAP_EDGE",EDGE,{"disambiguationData":[OSD([sQuery(id+"F6.wireOp",EDGE,"E183.right")])],"isStart":false});
            var Q1;
            Q1=makeQuery(id+"F7.opExtrude","CAP_EDGE",EDGE,{"disambiguationData":[OSD([sQuery(id+"F6.wireOp",EDGE,"E183.left")])],"isStart":false});
            chamfer(context, id + "F8", {"entities" : qUnion([Q0, Q1]), "chamferType" : ChamferType.TWO_OFFSETS, "width1" : 2 * mm, "oppositeDirection" : false, "width2" : 1 * mm, "tangentPropagation" : true});
        }
        {
            var Q0;
            Q0=qCreatedBy(makeId("Top.planeOp"),FACE);
            var sketch = newSketch(context, id + "F9", { "sketchPlane" : qUnion([Q0])});
            skCircle(sketch, "E184", {"center": v(51.07, 26.44) * mm, "radius": 4.75 * mm});
            skSolve(sketch);
        }
        {
            var Q0;
            Q0 = qSketchRegion(id + "F9", true);
            extrude(context, id + "F10", {"entities" : qUnion([Q0]), "operationType" : NewBodyOperationType.ADD, "depth" : 2 * mm, "offsetDistance" : 25 * mm});
        }
        {
            var Q0;
            Q0=makeQuery(id+"F10.boolean.opBoolean","MERGE",FACE,{"derivedFrom":[makeQuery(id+"F1.opExtrude","CAP_FACE",FACE,{"disambiguationData":[OSD([sQuery(id+"F0.wireOp",EDGE,"E0"),sQuery(id+"F0.wireOp",EDGE,"E1"),sQuery(id+"F0.wireOp",EDGE,"E2"),sQuery(id+"F0.wireOp",EDGE,"E3"),sQuery(id+"F0.wireOp",EDGE,"E4"),sQuery(id+"F0.wireOp",EDGE,"E5"),sQuery(id+"F0.wireOp",EDGE,"E6"),sQuery(id+"F0.wireOp",EDGE,"E7"),sQuery(id+"F0.wireOp",EDGE,"E8"),sQuery(id+"F0.wireOp",EDGE,"E9"),sQuery(id+"F0.wireOp",EDGE,"E10"),sQuery(id+"F0.wireOp",EDGE,"E11"),sQuery(id+"F0.wireOp",EDGE,"E12"),sQuery(id+"F0.wireOp",EDGE,"E13"),sQuery(id+"F0.wireOp",EDGE,"E14"),sQuery(id+"F0.wireOp",EDGE,"E15"),sQuery(id+"F0.wireOp",EDGE,"E16"),sQuery(id+"F0.wireOp",EDGE,"E17"),sQuery(id+"F0.wireOp",EDGE,"E18"),sQuery(id+"F0.wireOp",EDGE,"E19"),sQuery(id+"F0.wireOp",EDGE,"E20"),sQuery(id+"F0.wireOp",EDGE,"E21"),sQuery(id+"F0.wireOp",EDGE,"E22"),sQuery(id+"F0.wireOp",EDGE,"E23"),sQuery(id+"F0.wireOp",EDGE,"E24"),sQuery(id+"F0.wireOp",EDGE,"E25"),sQuery(id+"F0.wireOp",EDGE,"E26"),sQuery(id+"F0.wireOp",EDGE,"E27"),sQuery(id+"F0.wireOp",EDGE,"E28"),sQuery(id+"F0.wireOp",EDGE,"E29"),sQuery(id+"F0.wireOp",EDGE,"E30"),sQuery(id+"F0.wireOp",EDGE,"E31"),sQuery(id+"F0.wireOp",EDGE,"E32"),sQuery(id+"F0.wireOp",EDGE,"E33"),sQuery(id+"F0.wireOp",EDGE,"E34"),sQuery(id+"F0.wireOp",EDGE,"E35"),sQuery(id+"F0.wireOp",EDGE,"E36"),sQuery(id+"F0.wireOp",EDGE,"E37"),sQuery(id+"F0.wireOp",EDGE,"E38"),sQuery(id+"F0.wireOp",EDGE,"E39"),sQuery(id+"F0.wireOp",EDGE,"E40"),sQuery(id+"F0.wireOp",EDGE,"E41"),sQuery(id+"F0.wireOp",EDGE,"E42"),sQuery(id+"F0.wireOp",EDGE,"E43"),sQuery(id+"F0.wireOp",EDGE,"E44"),sQuery(id+"F0.wireOp",EDGE,"E45"),sQuery(id+"F0.wireOp",EDGE,"E46"),sQuery(id+"F0.wireOp",EDGE,"E47"),sQuery(id+"F0.wireOp",EDGE,"E48"),sQuery(id+"F0.wireOp",EDGE,"E49"),sQuery(id+"F0.wireOp",EDGE,"E50"),sQuery(id+"F0.wireOp",EDGE,"E51"),sQuery(id+"F0.wireOp",EDGE,"E52"),sQuery(id+"F0.wireOp",EDGE,"E53"),sQuery(id+"F0.wireOp",EDGE,"E54"),sQuery(id+"F0.wireOp",EDGE,"E55"),sQuery(id+"F0.wireOp",EDGE,"E56"),sQuery(id+"F0.wireOp",EDGE,"E57"),sQuery(id+"F0.wireOp",EDGE,"E58"),sQuery(id+"F0.wireOp",EDGE,"E59"),sQuery(id+"F0.wireOp",EDGE,"E60"),sQuery(id+"F0.wireOp",EDGE,"E61"),sQuery(id+"F0.wireOp",EDGE,"E62"),sQuery(id+"F0.wireOp",EDGE,"E63"),sQuery(id+"F0.wireOp",EDGE,"E64"),sQuery(id+"F0.wireOp",EDGE,"E65"),sQuery(id+"F0.wireOp",EDGE,"E66"),sQuery(id+"F0.wireOp",EDGE,"E67"),sQuery(id+"F0.wireOp",EDGE,"E68"),sQuery(id+"F0.wireOp",EDGE,"E69"),sQuery(id+"F0.wireOp",EDGE,"E70"),sQuery(id+"F0.wireOp",EDGE,"E71"),sQuery(id+"F0.wireOp",EDGE,"E72"),sQuery(id+"F0.wireOp",EDGE,"E73"),sQuery(id+"F0.wireOp",EDGE,"E74"),sQuery(id+"F0.wireOp",EDGE,"E75"),sQuery(id+"F0.wireOp",EDGE,"E76"),sQuery(id+"F0.wireOp",EDGE,"E77"),sQuery(id+"F0.wireOp",EDGE,"E78"),sQuery(id+"F0.wireOp",EDGE,"E79"),sQuery(id+"F0.wireOp",EDGE,"E80"),sQuery(id+"F0.wireOp",EDGE,"E81"),sQuery(id+"F0.wireOp",EDGE,"E82"),sQuery(id+"F0.wireOp",EDGE,"E83"),sQuery(id+"F0.wireOp",EDGE,"E84"),sQuery(id+"F0.wireOp",EDGE,"E85"),sQuery(id+"F0.wireOp",EDGE,"E86"),sQuery(id+"F0.wireOp",EDGE,"E87"),sQuery(id+"F0.wireOp",EDGE,"E88"),sQuery(id+"F0.wireOp",EDGE,"E89"),sQuery(id+"F0.wireOp",EDGE,"E90"),sQuery(id+"F0.wireOp",EDGE,"E91"),sQuery(id+"F0.wireOp",EDGE,"E92"),sQuery(id+"F0.wireOp",EDGE,"E93"),sQuery(id+"F0.wireOp",EDGE,"E94"),sQuery(id+"F0.wireOp",EDGE,"E95"),sQuery(id+"F0.wireOp",EDGE,"E96")])],"isStart":false}),makeQuery(id+"F10.opExtrude","CAP_FACE",FACE,{"disambiguationData":[OSD([sQuery(id+"F9.wireOp",EDGE,"E184")])],"isStart":false})]});
            var sketch = newSketch(context, id + "F11", { "sketchPlane" : qUnion([Q0])});
            skCircle(sketch, "E185", {"center": v(51.07, 26.44) * mm, "radius": 3.1 * mm});
            skSolve(sketch);
        }
        {
            var Q0;
            Q0 = qSketchRegion(id + "F11", true);
            extrude(context, id + "F12", {"entities" : qUnion([Q0]), "operationType" : NewBodyOperationType.REMOVE, "oppositeDirection" : true, "depth" : 25 * mm, "offsetDistance" : 25 * mm});
        }
        {
            var Q0;
            Q0=makeQuery(id+"F10.opExtrude","CAP_EDGE",EDGE,{"disambiguationData":[OSD([sQuery(id+"F9.wireOp",EDGE,"E184")])],"isStart":false});
            var Q1;
            Q1=makeQuery(id+"F12.boolean.opBoolean","COPY",EDGE,{"derivedFrom":makeQuery(id+"F12.opExtrude","CAP_EDGE",EDGE,{"disambiguationData":[OSD([sQuery(id+"F11.wireOp",EDGE,"E185")])],"isStart":true})});
            var Q2;
            Q2=makeQuery(id+"F12.boolean.opBoolean","INTERSECT",EDGE,{"derivedFrom":[makeQuery(id+"F10.boolean.opBoolean","MERGE",FACE,{"derivedFrom":[makeQuery(id+"F1.opExtrude","CAP_FACE",FACE,{"disambiguationData":[OSD([sQuery(id+"F0.wireOp",EDGE,"E0"),sQuery(id+"F0.wireOp",EDGE,"E1"),sQuery(id+"F0.wireOp",EDGE,"E2"),sQuery(id+"F0.wireOp",EDGE,"E3"),sQuery(id+"F0.wireOp",EDGE,"E4"),sQuery(id+"F0.wireOp",EDGE,"E5"),sQuery(id+"F0.wireOp",EDGE,"E6"),sQuery(id+"F0.wireOp",EDGE,"E7"),sQuery(id+"F0.wireOp",EDGE,"E8"),sQuery(id+"F0.wireOp",EDGE,"E9"),sQuery(id+"F0.wireOp",EDGE,"E10"),sQuery(id+"F0.wireOp",EDGE,"E11"),sQuery(id+"F0.wireOp",EDGE,"E12"),sQuery(id+"F0.wireOp",EDGE,"E13"),sQuery(id+"F0.wireOp",EDGE,"E14"),sQuery(id+"F0.wireOp",EDGE,"E15"),sQuery(id+"F0.wireOp",EDGE,"E16"),sQuery(id+"F0.wireOp",EDGE,"E17"),sQuery(id+"F0.wireOp",EDGE,"E18"),sQuery(id+"F0.wireOp",EDGE,"E19"),sQuery(id+"F0.wireOp",EDGE,"E20"),sQuery(id+"F0.wireOp",EDGE,"E21"),sQuery(id+"F0.wireOp",EDGE,"E22"),sQuery(id+"F0.wireOp",EDGE,"E23"),sQuery(id+"F0.wireOp",EDGE,"E24"),sQuery(id+"F0.wireOp",EDGE,"E25"),sQuery(id+"F0.wireOp",EDGE,"E26"),sQuery(id+"F0.wireOp",EDGE,"E27"),sQuery(id+"F0.wireOp",EDGE,"E28"),sQuery(id+"F0.wireOp",EDGE,"E29"),sQuery(id+"F0.wireOp",EDGE,"E30"),sQuery(id+"F0.wireOp",EDGE,"E31"),sQuery(id+"F0.wireOp",EDGE,"E32"),sQuery(id+"F0.wireOp",EDGE,"E33"),sQuery(id+"F0.wireOp",EDGE,"E34"),sQuery(id+"F0.wireOp",EDGE,"E35"),sQuery(id+"F0.wireOp",EDGE,"E36"),sQuery(id+"F0.wireOp",EDGE,"E37"),sQuery(id+"F0.wireOp",EDGE,"E38"),sQuery(id+"F0.wireOp",EDGE,"E39"),sQuery(id+"F0.wireOp",EDGE,"E40"),sQuery(id+"F0.wireOp",EDGE,"E41"),sQuery(id+"F0.wireOp",EDGE,"E42"),sQuery(id+"F0.wireOp",EDGE,"E43"),sQuery(id+"F0.wireOp",EDGE,"E44"),sQuery(id+"F0.wireOp",EDGE,"E45"),sQuery(id+"F0.wireOp",EDGE,"E46"),sQuery(id+"F0.wireOp",EDGE,"E47"),sQuery(id+"F0.wireOp",EDGE,"E48"),sQuery(id+"F0.wireOp",EDGE,"E49"),sQuery(id+"F0.wireOp",EDGE,"E50"),sQuery(id+"F0.wireOp",EDGE,"E51"),sQuery(id+"F0.wireOp",EDGE,"E52"),sQuery(id+"F0.wireOp",EDGE,"E53"),sQuery(id+"F0.wireOp",EDGE,"E54"),sQuery(id+"F0.wireOp",EDGE,"E55"),sQuery(id+"F0.wireOp",EDGE,"E56"),sQuery(id+"F0.wireOp",EDGE,"E57"),sQuery(id+"F0.wireOp",EDGE,"E58"),sQuery(id+"F0.wireOp",EDGE,"E59"),sQuery(id+"F0.wireOp",EDGE,"E60"),sQuery(id+"F0.wireOp",EDGE,"E61"),sQuery(id+"F0.wireOp",EDGE,"E62"),sQuery(id+"F0.wireOp",EDGE,"E63"),sQuery(id+"F0.wireOp",EDGE,"E64"),sQuery(id+"F0.wireOp",EDGE,"E65"),sQuery(id+"F0.wireOp",EDGE,"E66"),sQuery(id+"F0.wireOp",EDGE,"E67"),sQuery(id+"F0.wireOp",EDGE,"E68"),sQuery(id+"F0.wireOp",EDGE,"E69"),sQuery(id+"F0.wireOp",EDGE,"E70"),sQuery(id+"F0.wireOp",EDGE,"E71"),sQuery(id+"F0.wireOp",EDGE,"E72"),sQuery(id+"F0.wireOp",EDGE,"E73"),sQuery(id+"F0.wireOp",EDGE,"E74"),sQuery(id+"F0.wireOp",EDGE,"E75"),sQuery(id+"F0.wireOp",EDGE,"E76"),sQuery(id+"F0.wireOp",EDGE,"E77"),sQuery(id+"F0.wireOp",EDGE,"E78"),sQuery(id+"F0.wireOp",EDGE,"E79"),sQuery(id+"F0.wireOp",EDGE,"E80"),sQuery(id+"F0.wireOp",EDGE,"E81"),sQuery(id+"F0.wireOp",EDGE,"E82"),sQuery(id+"F0.wireOp",EDGE,"E83"),sQuery(id+"F0.wireOp",EDGE,"E84"),sQuery(id+"F0.wireOp",EDGE,"E85"),sQuery(id+"F0.wireOp",EDGE,"E86"),sQuery(id+"F0.wireOp",EDGE,"E87"),sQuery(id+"F0.wireOp",EDGE,"E88"),sQuery(id+"F0.wireOp",EDGE,"E89"),sQuery(id+"F0.wireOp",EDGE,"E90"),sQuery(id+"F0.wireOp",EDGE,"E91"),sQuery(id+"F0.wireOp",EDGE,"E92"),sQuery(id+"F0.wireOp",EDGE,"E93"),sQuery(id+"F0.wireOp",EDGE,"E94"),sQuery(id+"F0.wireOp",EDGE,"E95"),sQuery(id+"F0.wireOp",EDGE,"E96")])],"isStart":true}),makeQuery(id+"F10.opExtrude","CAP_FACE",FACE,{"disambiguationData":[OSD([sQuery(id+"F9.wireOp",EDGE,"E184")])],"isStart":true})]}),makeQuery(id+"F12.opExtrude","SWEPT_FACE",FACE,{"disambiguationData":[OSD([sQuery(id+"F11.wireOp",EDGE,"E185")])]})]});
            var Q3;
            Q3=makeQuery(id+"F10.opExtrude","CAP_EDGE",EDGE,{"disambiguationData":[OSD([sQuery(id+"F9.wireOp",EDGE,"E184")])],"isStart":true});
            fillet(context, id + "F13", {"entities" : qUnion([Q0, Q1, Q2, Q3]), "radius" : .5 * mm, "tangentPropagation" : true, "allowEdgeOverflow" : false});
        }
    });
